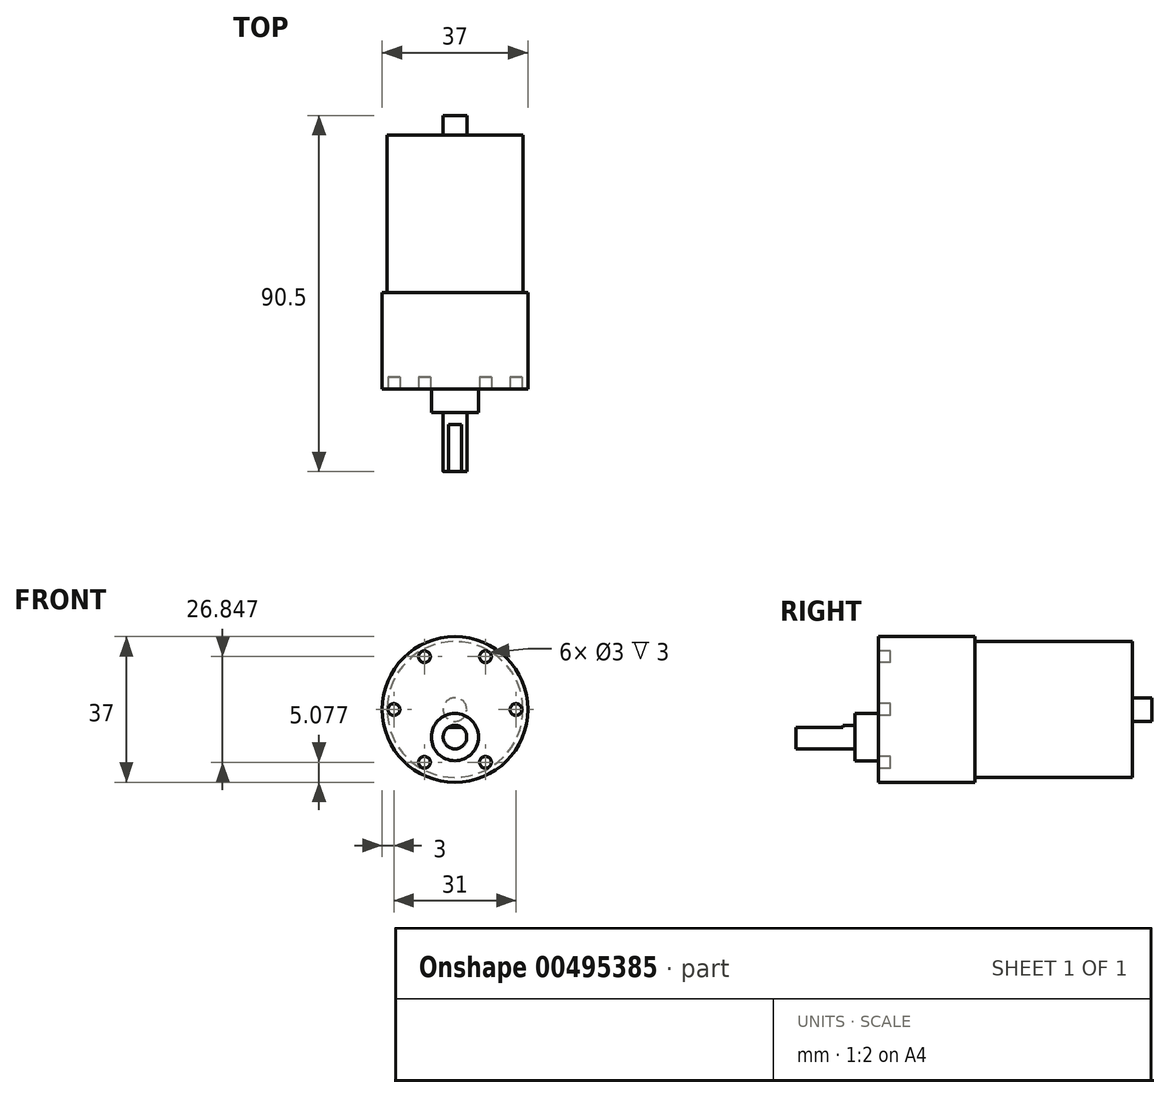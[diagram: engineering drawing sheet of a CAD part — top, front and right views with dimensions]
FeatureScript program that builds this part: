
annotation { "Feature Type Name" : "Feature", "Feature Type Description" : "" }
export const myFeature = defineFeature(function(context is Context, id is Id, definition is map)
    precondition{}
    {
        {
            var Q0;
            Q0=qCreatedBy(makeId("Front.planeOp"),FACE);
            var sketch = newSketch(context, id + "F0", { "sketchPlane" : qUnion([Q0])});
            skCircle(sketch, "E0", {"center": v(0, 0) * mm, "radius": 18.5 * mm});
            skSolve(sketch);
        }
        {
            var Q0;
            Q0=qSketchRegion(id+"F0",true);
            extrude(context, id + "F1", {"entities" : qUnion([Q0]), "depth" : 24.5 * mm});
        }
        {
            var Q0;
            Q0=makeQuery(id+"F1.opExtrude","CAP_FACE",FACE,{"disambiguationData":[OSD([sQuery(id+"F0.wireOp",EDGE,"E0")])],"isStart":true});
            var sketch = newSketch(context, id + "F2", { "sketchPlane" : qUnion([Q0])});
            skCircle(sketch, "E1", {"center": v(0, 0) * mm, "radius": 17.25 * mm});
            skSolve(sketch);
        }
        {
            var Q0;
            Q0=qSketchRegion(id+"F2",true);
            extrude(context, id + "F3", {"entities" : qUnion([Q0]), "operationType" : NewBodyOperationType.ADD, "depth" : 40 * mm});
        }
        {
            var Q0;
            Q0=makeQuery(id+"F3.opExtrude","CAP_FACE",FACE,{"disambiguationData":[OSD([sQuery(id+"F2.wireOp",EDGE,"E1")])],"isStart":false});
            var sketch = newSketch(context, id + "F4", { "sketchPlane" : qUnion([Q0])});
            skCircle(sketch, "E2", {"center": v(0, 0) * mm, "radius": 3 * mm});
            skSolve(sketch);
        }
        {
            var Q0;
            Q0=qSketchRegion(id+"F4",true);
            extrude(context, id + "F5", {"entities" : qUnion([Q0]), "operationType" : NewBodyOperationType.ADD, "depth" : 5 * mm});
        }
        {
            var Q0;
            Q0=makeQuery(id+"F1.opExtrude","CAP_FACE",FACE,{"disambiguationData":[OSD([sQuery(id+"F0.wireOp",EDGE,"E0")])],"isStart":false});
            var sketch = newSketch(context, id + "F6", { "sketchPlane" : qUnion([Q0])});
            skCircle(sketch, "E3.cCircle", {"center": v(0, 0) * mm, "radius": 15.5 * mm, "construction": true});
            skLineSegment(sketch, "E3.0", {"start": v(7.75, 13.42) * mm, "end": v(15.5, 0) * mm, "construction": true});
            skLineSegment(sketch, "E3.1", {"start": v(15.5, 0) * mm, "end": v(7.75, -13.42) * mm, "construction": true});
            skLineSegment(sketch, "E3.2", {"start": v(7.75, -13.42) * mm, "end": v(-7.75, -13.42) * mm, "construction": true});
            skLineSegment(sketch, "E3.3", {"start": v(-7.75, -13.42) * mm, "end": v(-15.5, 0) * mm, "construction": true});
            skLineSegment(sketch, "E3.4", {"start": v(-15.5, 0) * mm, "end": v(-7.75, 13.42) * mm, "construction": true});
            skLineSegment(sketch, "E3.5", {"start": v(-7.75, 13.42) * mm, "end": v(7.75, 13.42) * mm, "construction": true});
            skCircle(sketch, "E4", {"center": v(7.75, 13.42) * mm, "radius": 1.5 * mm});
            skCircle(sketch, "E5", {"center": v(-7.75, 13.42) * mm, "radius": 1.5 * mm});
            skCircle(sketch, "E6", {"center": v(-15.5, 0) * mm, "radius": 1.5 * mm});
            skCircle(sketch, "E7", {"center": v(-7.75, -13.42) * mm, "radius": 1.5 * mm});
            skCircle(sketch, "E8", {"center": v(7.75, -13.42) * mm, "radius": 1.5 * mm});
            skCircle(sketch, "E9", {"center": v(15.5, 0) * mm, "radius": 1.5 * mm});
            skSolve(sketch);
        }
        {
            var Q0;
            Q0=qSketchRegion(id+"F6",true);
            extrude(context, id + "F7", {"entities" : qUnion([Q0]), "operationType" : NewBodyOperationType.REMOVE, "oppositeDirection" : true, "depth" : 3 * mm});
        }
        {
            var Q0;
            Q0=makeQuery(id+"F1.opExtrude","CAP_FACE",FACE,{"disambiguationData":[OSD([sQuery(id+"F0.wireOp",EDGE,"E0")])],"isStart":false});
            var sketch = newSketch(context, id + "F8", { "sketchPlane" : qUnion([Q0])});
            skLineSegment(sketch, "E10", {"start": v(0, 18.5) * mm, "end": v(0, -18.5) * mm, "construction": true});
            skCircle(sketch, "E11", {"center": v(0, -7) * mm, "radius": 6 * mm});
            skPoint(sketch, "E12", {"position": v(0, 0) * mm});
            skSolve(sketch);
        }
        {
            var Q0;
            Q0=qSketchRegion(id+"F8",true);
            extrude(context, id + "F9", {"entities" : qUnion([Q0]), "operationType" : NewBodyOperationType.ADD, "depth" : 6 * mm});
        }
        {
            var Q0;
            Q0=makeQuery(id+"F9.opExtrude","CAP_FACE",FACE,{"disambiguationData":[OSD([sQuery(id+"F8.wireOp",EDGE,"E11")])],"isStart":false});
            var sketch = newSketch(context, id + "F10", { "sketchPlane" : qUnion([Q0])});
            skCircle(sketch, "E13", {"center": v(0, -7) * mm, "radius": 3 * mm});
            skSolve(sketch);
        }
        {
            var Q0;
            Q0=qSketchRegion(id+"F10",true);
            var Q1;
            Q1=makeQuery(id+"F1.opExtrude","CAP_FACE",FACE,{"disambiguationData":[OSD([sQuery(id+"F0.wireOp",EDGE,"E0")])],"isStart":false});
            extrude(context, id + "F11", {"entities" : qUnion([Q0]), "operationType" : NewBodyOperationType.ADD, "endBoundEntity" : qUnion([Q1]), "depth" : 15 * mm});
        }
        {
            var Q0;
            Q0=makeQuery(id+"F11.opExtrude","CAP_FACE",FACE,{"disambiguationData":[OSD([sQuery(id+"F10.wireOp",EDGE,"E13")])],"isStart":false});
            var sketch = newSketch(context, id + "F12", { "sketchPlane" : qUnion([Q0])});
            skLineSegment(sketch, "E14", {"start": v(-1.66, -4.5) * mm, "end": v(1.66, -4.5) * mm});
            skArc(sketch, "E15.0", {"start": v(1.66, -4.5) * mm, "mid": v(0, -4) * mm, "end": v(-1.66, -4.5) * mm});
            skLineSegment(sketch, "E16", {"start": v(0, -4.5) * mm, "end": v(0, -10) * mm, "construction": true});
            skSolve(sketch);
        }
        {
            var Q0;
            Q0=qSketchRegion(id+"F12",true);
            extrude(context, id + "F13", {"entities" : qUnion([Q0]), "operationType" : NewBodyOperationType.REMOVE, "oppositeDirection" : true, "depth" : 12 * mm});
        }
    });
